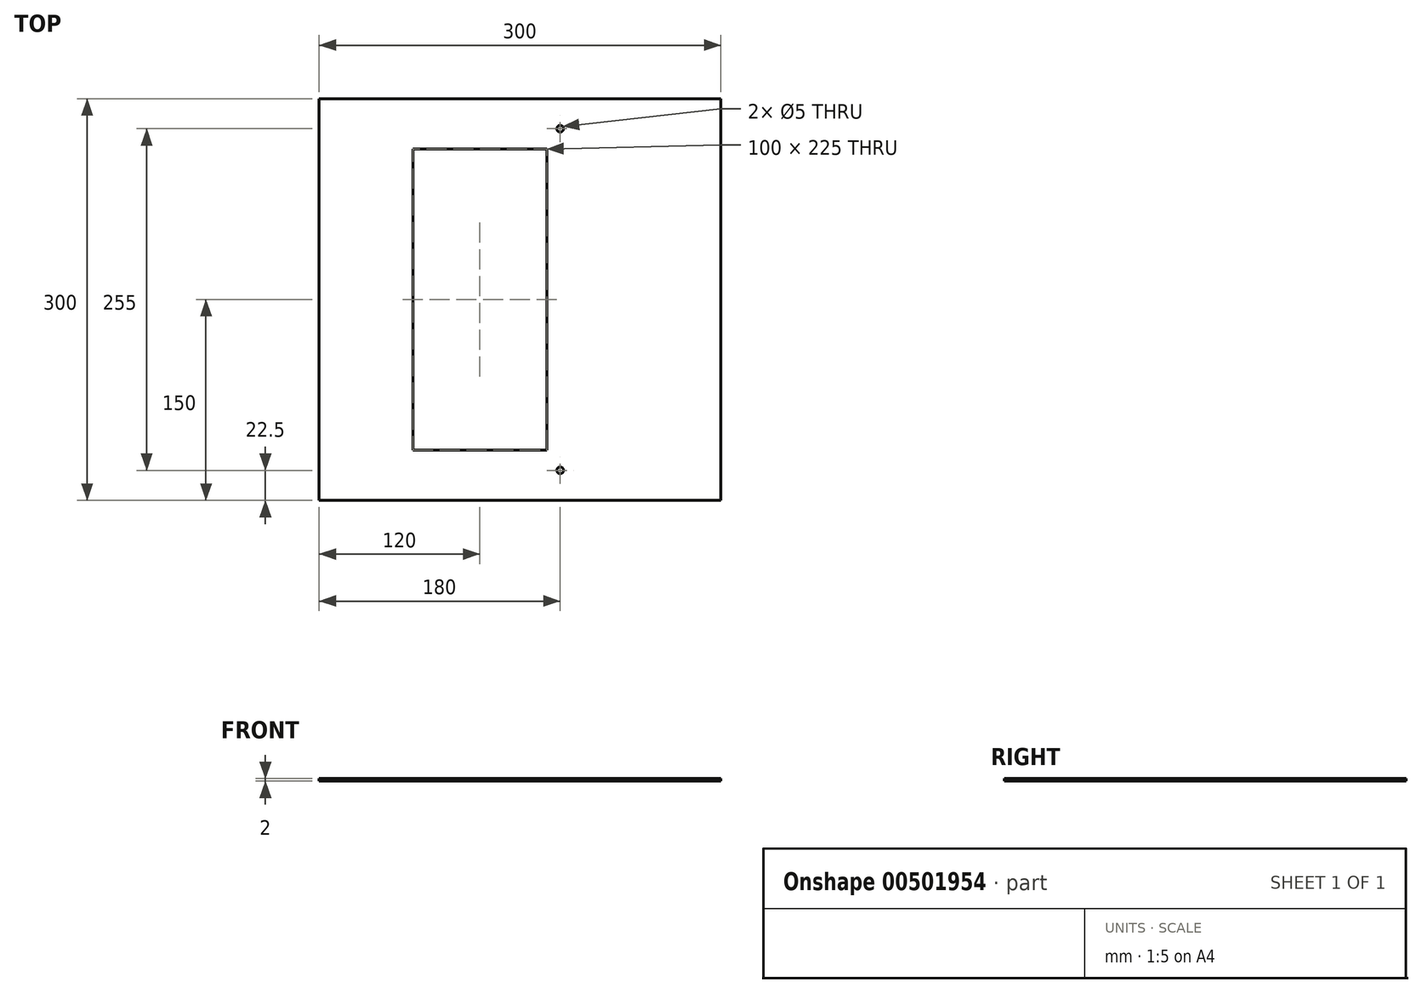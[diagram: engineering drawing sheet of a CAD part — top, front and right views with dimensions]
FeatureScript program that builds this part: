
annotation { "Feature Type Name" : "Feature", "Feature Type Description" : "" }
export const myFeature = defineFeature(function(context is Context, id is Id, definition is map)
    precondition{}
    {
        {
            var Q0;
            Q0=qCreatedBy(makeId("Top.planeOp"),FACE);
            var sketch = newSketch(context, id + "F0", { "sketchPlane" : qUnion([Q0])});
            skLineSegment(sketch, "E0.bottom", {"start": v(150, 150) * mm, "end": v(-150, 150) * mm});
            skLineSegment(sketch, "E0.top", {"start": v(150, -150) * mm, "end": v(-150, -150) * mm});
            skLineSegment(sketch, "E0.left", {"start": v(150, 150) * mm, "end": v(150, -150) * mm});
            skLineSegment(sketch, "E0.right", {"start": v(-150, 150) * mm, "end": v(-150, -150) * mm});
            skPoint(sketch, "E0.middle", {"position": v(0, 0) * mm});
            skLineSegment(sketch, "E1.bottom", {"start": v(-80, 112.5) * mm, "end": v(20, 112.5) * mm});
            skLineSegment(sketch, "E1.top", {"start": v(-80, -112.5) * mm, "end": v(20, -112.5) * mm});
            skLineSegment(sketch, "E1.left", {"start": v(-80, 112.5) * mm, "end": v(-80, -112.5) * mm});
            skLineSegment(sketch, "E1.right", {"start": v(20, 112.5) * mm, "end": v(20, -112.5) * mm});
            skPoint(sketch, "E2", {"position": v(20, 0) * mm});
            skCircle(sketch, "E3", {"center": v(30, 127.5) * mm, "radius": 2.5 * mm});
            skCircle(sketch, "E4.MirrorC", {"center": v(30, -127.5) * mm, "radius": 2.5 * mm});
            skSolve(sketch);
        }
        {
            var Q0;
            Q0=makeQuery(id+"F0.imprint","IMPRINT",FACE,{"disambiguationData":[TD([[makeQuery(id+"F0.imprint","IMPRINT",EDGE,{"derivedFrom":sQuery(id+"F0.wireOp",EDGE,"E0.bottom")}),1.0]])]});
            extrude(context, id + "F1", {"entities" : qUnion([Q0]), "depth" : 2 * mm, "symmetric" : true});
        }
    });
